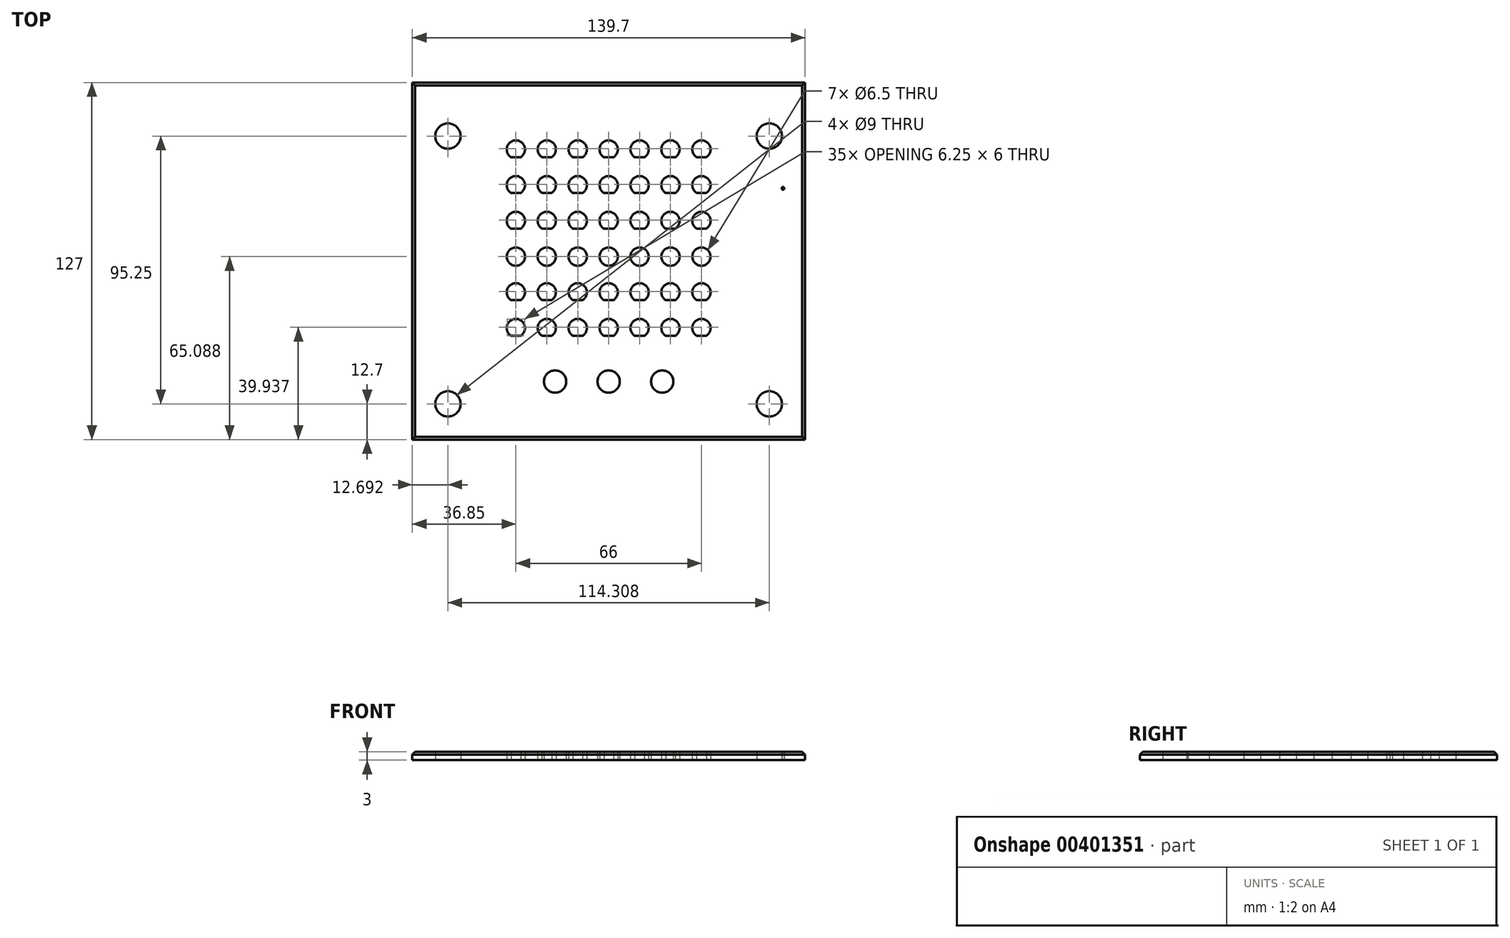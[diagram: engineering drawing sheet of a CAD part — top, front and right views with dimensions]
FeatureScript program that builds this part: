
annotation { "Feature Type Name" : "Feature", "Feature Type Description" : "" }
export const myFeature = defineFeature(function(context is Context, id is Id, definition is map)
    precondition{}
    {
        {
            var Q0;
            Q0=qCreatedBy(makeId("Top.planeOp"),FACE);
            var sketch = newSketch(context, id + "F0", { "sketchPlane" : qUnion([Q0])});
            skLineSegment(sketch, "E0.bottom", {"start": v(69.85, -63.5) * mm, "end": v(-69.85, -63.5) * mm});
            skLineSegment(sketch, "E0.top", {"start": v(69.85, 63.5) * mm, "end": v(-69.85, 63.5) * mm});
            skLineSegment(sketch, "E0.left", {"start": v(69.85, -63.5) * mm, "end": v(69.85, 63.5) * mm});
            skLineSegment(sketch, "E0.right", {"start": v(-69.85, -63.5) * mm, "end": v(-69.85, 63.5) * mm});
            skPoint(sketch, "E0.middle", {"position": v(0, 0) * mm});
            skLineSegment(sketch, "E1", {"start": v(-36.63, 14.29) * mm, "end": v(37.18, 14.29) * mm, "construction": true});
            skLineSegment(sketch, "E2", {"start": v(-37.34, 1.59) * mm, "end": v(37.24, 1.59) * mm, "construction": true});
            skLineSegment(sketch, "E3", {"start": v(-37.24, -11.11) * mm, "end": v(37.24, -11.11) * mm, "construction": true});
            skLineSegment(sketch, "E4", {"start": v(-37.55, -23.81) * mm, "end": v(37.34, -23.81) * mm, "construction": true});
            skLineSegment(sketch, "E5", {"start": v(0, -38.04) * mm, "end": v(0, 63.5) * mm, "construction": true});
            skLineSegment(sketch, "E6", {"start": v(-11, -26.1) * mm, "end": v(-11, 63.5) * mm, "construction": true});
            skLineSegment(sketch, "E7", {"start": v(-22, -38.04) * mm, "end": v(-22, 63.5) * mm, "construction": true});
            skLineSegment(sketch, "E8", {"start": v(-33, -38.57) * mm, "end": v(-33, 63.5) * mm, "construction": true});
            skLineSegment(sketch, "E9", {"start": v(11, -39.12) * mm, "end": v(11, 63.5) * mm, "construction": true});
            skLineSegment(sketch, "E10", {"start": v(22, -39.12) * mm, "end": v(22, 63.5) * mm, "construction": true});
            skLineSegment(sketch, "E11", {"start": v(33, -26.65) * mm, "end": v(33, 63.5) * mm, "construction": true});
            skLineSegment(sketch, "E12", {"start": v(-36.74, -42.86) * mm, "end": v(36.74, -42.86) * mm, "construction": true});
            skPoint(sketch, "E13", {"position": v(0, -42.86) * mm});
            skCircle(sketch, "E14", {"center": v(0, -42.86) * mm, "radius": 3.97 * mm});
            skCircle(sketch, "E15", {"center": v(19.05, -42.86) * mm, "radius": 3.97 * mm});
            skCircle(sketch, "E16", {"center": v(-19.05, -42.86) * mm, "radius": 3.97 * mm});
            skLineSegment(sketch, "E17.bottom", {"start": v(38.1, -38.1) * mm, "end": v(-38.1, -38.1) * mm, "construction": true});
            skLineSegment(sketch, "E17.left", {"start": v(38.1, -38.1) * mm, "end": v(38.1, 38.1) * mm, "construction": true});
            skLineSegment(sketch, "E17.right", {"start": v(-38.1, -38.1) * mm, "end": v(-38.1, 38.1) * mm, "construction": true});
            skCircle(sketch, "E18", {"center": v(-57.15, -50.8) * mm, "radius": 4.5 * mm});
            skLineSegment(sketch, "E19", {"start": v(-57.15, -47.32) * mm, "end": v(-57.15, 45.96) * mm, "construction": true});
            skLineSegment(sketch, "E20", {"start": v(-65.5, -50.8) * mm, "end": v(68.65, -50.8) * mm, "construction": true});
            skLineSegment(sketch, "E21", {"start": v(57.15, -46.6) * mm, "end": v(57.15, 47.13) * mm, "construction": true});
            skLineSegment(sketch, "E22", {"start": v(-64.4, 39.69) * mm, "end": v(66.43, 39.69) * mm, "construction": true});
            skCircle(sketch, "E23", {"center": v(57.15, -50.8) * mm, "radius": 4.5 * mm});
            skLineSegment(sketch, "E24", {"start": v(-36.54, 26.99) * mm, "end": v(36.58, 26.99) * mm, "construction": true});
            skLineSegment(sketch, "E25", {"start": v(-36.46, 39.69) * mm, "end": v(36.58, 39.69) * mm, "construction": true});
            skCircle(sketch, "E26", {"center": v(-33, 39.69) * mm, "radius": 3.25 * mm});
            skLineSegment(sketch, "E27", {"start": v(-67.5, 46.04) * mm, "end": v(65.6, 46.04) * mm, "construction": true});
            skLineSegment(sketch, "E28", {"start": v(-34.73, 36.94) * mm, "end": v(-31.27, 36.94) * mm});
            skCircle(sketch, "E29", {"center": v(-22, 39.69) * mm, "radius": 3.25 * mm});
            skLineSegment(sketch, "E30", {"start": v(-23.73, 36.94) * mm, "end": v(-20.27, 36.94) * mm});
            skCircle(sketch, "E31", {"center": v(-11, 39.69) * mm, "radius": 3.25 * mm});
            skLineSegment(sketch, "E32", {"start": v(-12.73, 36.94) * mm, "end": v(-9.27, 36.94) * mm});
            skCircle(sketch, "E33", {"center": v(0, 39.69) * mm, "radius": 3.25 * mm});
            skLineSegment(sketch, "E34", {"start": v(-1.73, 36.94) * mm, "end": v(1.73, 36.94) * mm});
            skPoint(sketch, "E35", {"position": v(1.02, 39.69) * mm});
            skCircle(sketch, "E36", {"center": v(11, 39.69) * mm, "radius": 3.25 * mm});
            skLineSegment(sketch, "E37", {"start": v(9.27, 36.94) * mm, "end": v(12.73, 36.94) * mm});
            skCircle(sketch, "E38", {"center": v(22, 39.69) * mm, "radius": 3.25 * mm});
            skLineSegment(sketch, "E39", {"start": v(20.27, 36.94) * mm, "end": v(23.73, 36.94) * mm});
            skCircle(sketch, "E40", {"center": v(33, 39.69) * mm, "radius": 3.25 * mm});
            skLineSegment(sketch, "E41", {"start": v(31.27, 36.94) * mm, "end": v(34.73, 36.94) * mm});
            skCircle(sketch, "E42", {"center": v(-33, 26.99) * mm, "radius": 3.25 * mm});
            skLineSegment(sketch, "E43", {"start": v(-34.73, 24.24) * mm, "end": v(-31.27, 24.24) * mm});
            skCircle(sketch, "E44", {"center": v(-22, 26.99) * mm, "radius": 3.25 * mm});
            skLineSegment(sketch, "E45", {"start": v(-23.73, 24.24) * mm, "end": v(-20.27, 24.24) * mm});
            skCircle(sketch, "E46", {"center": v(-11, 26.99) * mm, "radius": 3.25 * mm});
            skLineSegment(sketch, "E47", {"start": v(-12.73, 24.24) * mm, "end": v(-9.27, 24.24) * mm});
            skCircle(sketch, "E48", {"center": v(0, 26.99) * mm, "radius": 3.25 * mm});
            skLineSegment(sketch, "E49", {"start": v(-1.73, 24.24) * mm, "end": v(1.73, 24.24) * mm});
            skCircle(sketch, "E50", {"center": v(11, 26.99) * mm, "radius": 3.25 * mm});
            skLineSegment(sketch, "E51", {"start": v(9.27, 24.24) * mm, "end": v(12.73, 24.24) * mm});
            skCircle(sketch, "E52", {"center": v(22, 26.99) * mm, "radius": 3.25 * mm});
            skLineSegment(sketch, "E53", {"start": v(20.27, 24.24) * mm, "end": v(23.73, 24.24) * mm});
            skCircle(sketch, "E54", {"center": v(33, 26.99) * mm, "radius": 3.25 * mm});
            skLineSegment(sketch, "E55", {"start": v(31.27, 24.24) * mm, "end": v(34.73, 24.24) * mm});
            skPoint(sketch, "E56", {"position": v(0.02, 26.99) * mm});
            skCircle(sketch, "E57", {"center": v(-11, 14.29) * mm, "radius": 3.25 * mm});
            skLineSegment(sketch, "E58", {"start": v(-12.73, 11.54) * mm, "end": v(-9.27, 11.54) * mm});
            skCircle(sketch, "E59", {"center": v(0, 14.29) * mm, "radius": 3.25 * mm});
            skLineSegment(sketch, "E60", {"start": v(-1.73, 11.54) * mm, "end": v(1.73, 11.54) * mm});
            skCircle(sketch, "E61", {"center": v(11, 14.29) * mm, "radius": 3.25 * mm});
            skLineSegment(sketch, "E62", {"start": v(9.27, 11.54) * mm, "end": v(12.73, 11.54) * mm});
            skCircle(sketch, "E63", {"center": v(22, 14.29) * mm, "radius": 3.25 * mm});
            skLineSegment(sketch, "E64", {"start": v(20.27, 11.54) * mm, "end": v(23.73, 11.54) * mm});
            skCircle(sketch, "E65", {"center": v(33, 14.29) * mm, "radius": 3.25 * mm});
            skLineSegment(sketch, "E66", {"start": v(31.27, 11.54) * mm, "end": v(34.73, 11.54) * mm});
            skCircle(sketch, "E67", {"center": v(-33, 14.29) * mm, "radius": 3.25 * mm});
            skLineSegment(sketch, "E68", {"start": v(-34.73, 11.54) * mm, "end": v(-31.27, 11.54) * mm});
            skCircle(sketch, "E69", {"center": v(-22, 14.29) * mm, "radius": 3.25 * mm});
            skLineSegment(sketch, "E70", {"start": v(-23.73, 11.54) * mm, "end": v(-20.27, 11.54) * mm});
            skCircle(sketch, "E71", {"center": v(-11, -11.11) * mm, "radius": 3.25 * mm});
            skLineSegment(sketch, "E72", {"start": v(-12.73, -13.86) * mm, "end": v(-9.27, -13.86) * mm});
            skCircle(sketch, "E73", {"center": v(0, -11.11) * mm, "radius": 3.25 * mm});
            skLineSegment(sketch, "E74", {"start": v(-1.73, -13.86) * mm, "end": v(1.73, -13.86) * mm});
            skCircle(sketch, "E75", {"center": v(11, -11.11) * mm, "radius": 3.25 * mm});
            skLineSegment(sketch, "E76", {"start": v(9.27, -13.86) * mm, "end": v(12.73, -13.86) * mm});
            skCircle(sketch, "E77", {"center": v(22, -11.11) * mm, "radius": 3.25 * mm});
            skLineSegment(sketch, "E78", {"start": v(20.27, -13.86) * mm, "end": v(23.73, -13.86) * mm});
            skCircle(sketch, "E79", {"center": v(33, -11.11) * mm, "radius": 3.25 * mm});
            skLineSegment(sketch, "E80", {"start": v(31.27, -13.86) * mm, "end": v(34.73, -13.86) * mm});
            skCircle(sketch, "E81", {"center": v(-33, -11.11) * mm, "radius": 3.25 * mm});
            skLineSegment(sketch, "E82", {"start": v(-34.73, -13.86) * mm, "end": v(-31.27, -13.86) * mm});
            skCircle(sketch, "E83", {"center": v(-22, -11.11) * mm, "radius": 3.25 * mm});
            skLineSegment(sketch, "E84", {"start": v(-23.73, -13.86) * mm, "end": v(-20.27, -13.86) * mm});
            skCircle(sketch, "E85", {"center": v(-11, -23.81) * mm, "radius": 3.25 * mm});
            skLineSegment(sketch, "E86", {"start": v(-12.73, -26.56) * mm, "end": v(-9.27, -26.56) * mm});
            skCircle(sketch, "E87", {"center": v(0, -23.81) * mm, "radius": 3.25 * mm});
            skLineSegment(sketch, "E88", {"start": v(-1.73, -26.56) * mm, "end": v(1.73, -26.56) * mm});
            skCircle(sketch, "E89", {"center": v(11, -23.81) * mm, "radius": 3.25 * mm});
            skLineSegment(sketch, "E90", {"start": v(9.27, -26.56) * mm, "end": v(12.73, -26.56) * mm});
            skCircle(sketch, "E91", {"center": v(22, -23.81) * mm, "radius": 3.25 * mm});
            skLineSegment(sketch, "E92", {"start": v(20.27, -26.56) * mm, "end": v(23.73, -26.56) * mm});
            skCircle(sketch, "E93", {"center": v(33, -23.81) * mm, "radius": 3.25 * mm});
            skLineSegment(sketch, "E94", {"start": v(31.27, -26.56) * mm, "end": v(34.73, -26.56) * mm});
            skLineSegment(sketch, "E95", {"start": v(-33, -23.81) * mm, "end": v(-29.54, -23.81) * mm});
            skCircle(sketch, "E96", {"center": v(-22, -23.81) * mm, "radius": 3.25 * mm});
            skLineSegment(sketch, "E97", {"start": v(-23.73, -26.56) * mm, "end": v(-20.27, -26.56) * mm});
            skCircle(sketch, "E98", {"center": v(-33, -23.81) * mm, "radius": 3.25 * mm});
            skLineSegment(sketch, "E99", {"start": v(-34.73, -26.56) * mm, "end": v(-31.27, -26.56) * mm});
            skCircle(sketch, "E100", {"center": v(57.15, 44.45) * mm, "radius": 4.5 * mm});
            skCircle(sketch, "E101", {"center": v(61.99, 25.86) * mm, "radius": 0.47 * mm});
            skCircle(sketch, "E102", {"center": v(-57.16, 44.45) * mm, "radius": 4.5 * mm});
            skCircle(sketch, "E103", {"center": v(-11, 1.59) * mm, "radius": 3.25 * mm});
            skLineSegment(sketch, "E104", {"start": v(-12.73, -1.16) * mm, "end": v(-9.27, -1.16) * mm});
            skCircle(sketch, "E105", {"center": v(0, 1.59) * mm, "radius": 3.25 * mm});
            skLineSegment(sketch, "E106", {"start": v(-1.73, -1.16) * mm, "end": v(1.73, -1.16) * mm});
            skCircle(sketch, "E107", {"center": v(-33, 1.59) * mm, "radius": 3.25 * mm});
            skLineSegment(sketch, "E108", {"start": v(-34.73, -1.16) * mm, "end": v(-31.27, -1.16) * mm});
            skCircle(sketch, "E109", {"center": v(-22, 1.59) * mm, "radius": 3.25 * mm});
            skLineSegment(sketch, "E110", {"start": v(-23.73, -1.16) * mm, "end": v(-20.27, -1.16) * mm});
            skCircle(sketch, "E111", {"center": v(11, 1.59) * mm, "radius": 3.25 * mm});
            skLineSegment(sketch, "E112", {"start": v(9.27, -1.16) * mm, "end": v(12.73, -1.16) * mm});
            skCircle(sketch, "E113", {"center": v(22, 1.59) * mm, "radius": 3.25 * mm});
            skLineSegment(sketch, "E114", {"start": v(20.27, -1.16) * mm, "end": v(23.73, -1.16) * mm});
            skCircle(sketch, "E115", {"center": v(33, 1.59) * mm, "radius": 3.25 * mm});
            skLineSegment(sketch, "E116", {"start": v(31.27, -1.16) * mm, "end": v(34.73, -1.16) * mm});
            skSolve(sketch);
        }
        {
            var Q0;
            {var subQ0=sQuery(id+"F0.wireOp",EDGE,"E28");Q0=makeQuery(id+"F0.imprint","IMPRINT",FACE,{"disambiguationData":[TD([[makeQuery(id+"F0.imprint","IMPRINT",EDGE,{"derivedFrom":subQ0}),-1.0]])]});}
            var Q1;
            {var subQ0=sQuery(id+"F0.wireOp",EDGE,"E30");Q1=makeQuery(id+"F0.imprint","IMPRINT",FACE,{"disambiguationData":[TD([[makeQuery(id+"F0.imprint","IMPRINT",EDGE,{"derivedFrom":subQ0}),-1.0]])]});}
            var Q2;
            {var subQ0=sQuery(id+"F0.wireOp",EDGE,"E32");Q2=makeQuery(id+"F0.imprint","IMPRINT",FACE,{"disambiguationData":[TD([[makeQuery(id+"F0.imprint","IMPRINT",EDGE,{"derivedFrom":subQ0}),-1.0]])]});}
            var Q3;
            {var subQ0=sQuery(id+"F0.wireOp",EDGE,"E34");Q3=makeQuery(id+"F0.imprint","IMPRINT",FACE,{"disambiguationData":[TD([[makeQuery(id+"F0.imprint","IMPRINT",EDGE,{"derivedFrom":subQ0}),-1.0]])]});}
            var Q4;
            {var subQ0=sQuery(id+"F0.wireOp",EDGE,"E49");Q4=makeQuery(id+"F0.imprint","IMPRINT",FACE,{"disambiguationData":[TD([[makeQuery(id+"F0.imprint","IMPRINT",EDGE,{"derivedFrom":subQ0}),-1.0]])]});}
            var Q5;
            {var subQ0=sQuery(id+"F0.wireOp",EDGE,"E47");Q5=makeQuery(id+"F0.imprint","IMPRINT",FACE,{"disambiguationData":[TD([[makeQuery(id+"F0.imprint","IMPRINT",EDGE,{"derivedFrom":subQ0}),-1.0]])]});}
            var Q6;
            {var subQ0=sQuery(id+"F0.wireOp",EDGE,"E45");Q6=makeQuery(id+"F0.imprint","IMPRINT",FACE,{"disambiguationData":[TD([[makeQuery(id+"F0.imprint","IMPRINT",EDGE,{"derivedFrom":subQ0}),-1.0]])]});}
            var Q7;
            {var subQ0=sQuery(id+"F0.wireOp",EDGE,"E43");Q7=makeQuery(id+"F0.imprint","IMPRINT",FACE,{"disambiguationData":[TD([[makeQuery(id+"F0.imprint","IMPRINT",EDGE,{"derivedFrom":subQ0}),-1.0]])]});}
            var Q8;
            {var subQ0=sQuery(id+"F0.wireOp",EDGE,"E37");Q8=makeQuery(id+"F0.imprint","IMPRINT",FACE,{"disambiguationData":[TD([[makeQuery(id+"F0.imprint","IMPRINT",EDGE,{"derivedFrom":subQ0}),-1.0]])]});}
            var Q9;
            {var subQ0=sQuery(id+"F0.wireOp",EDGE,"E39");Q9=makeQuery(id+"F0.imprint","IMPRINT",FACE,{"disambiguationData":[TD([[makeQuery(id+"F0.imprint","IMPRINT",EDGE,{"derivedFrom":subQ0}),-1.0]])]});}
            var Q10;
            {var subQ0=sQuery(id+"F0.wireOp",EDGE,"E41");Q10=makeQuery(id+"F0.imprint","IMPRINT",FACE,{"disambiguationData":[TD([[makeQuery(id+"F0.imprint","IMPRINT",EDGE,{"derivedFrom":subQ0}),-1.0]])]});}
            var Q11;
            {var subQ0=sQuery(id+"F0.wireOp",EDGE,"E55");Q11=makeQuery(id+"F0.imprint","IMPRINT",FACE,{"disambiguationData":[TD([[makeQuery(id+"F0.imprint","IMPRINT",EDGE,{"derivedFrom":subQ0}),-1.0]])]});}
            var Q12;
            {var subQ0=sQuery(id+"F0.wireOp",EDGE,"E53");Q12=makeQuery(id+"F0.imprint","IMPRINT",FACE,{"disambiguationData":[TD([[makeQuery(id+"F0.imprint","IMPRINT",EDGE,{"derivedFrom":subQ0}),-1.0]])]});}
            var Q13;
            {var subQ0=sQuery(id+"F0.wireOp",EDGE,"E51");Q13=makeQuery(id+"F0.imprint","IMPRINT",FACE,{"disambiguationData":[TD([[makeQuery(id+"F0.imprint","IMPRINT",EDGE,{"derivedFrom":subQ0}),-1.0]])]});}
            var Q14;
            {var subQ0=sQuery(id+"F0.wireOp",EDGE,"E66");Q14=makeQuery(id+"F0.imprint","IMPRINT",FACE,{"disambiguationData":[TD([[makeQuery(id+"F0.imprint","IMPRINT",EDGE,{"derivedFrom":subQ0}),-1.0]])]});}
            var Q15;
            {var subQ0=sQuery(id+"F0.wireOp",EDGE,"5e4bbd30-fef1-421a-bd2a-7a05320ef783");Q15=makeQuery(id+"F0.imprint","IMPRINT",FACE,{"disambiguationData":[TD([[makeQuery(id+"F0.imprint","IMPRINT",EDGE,{"derivedFrom":subQ0}),-1.0]])]});}
            var Q16;
            {var subQ0=sQuery(id+"F0.wireOp",EDGE,"9f2551cd-3248-4687-9eb7-92e1bf331b68");Q16=makeQuery(id+"F0.imprint","IMPRINT",FACE,{"disambiguationData":[TD([[makeQuery(id+"F0.imprint","IMPRINT",EDGE,{"derivedFrom":subQ0}),-1.0]])]});}
            var Q17;
            {var subQ0=sQuery(id+"F0.wireOp",EDGE,"ff4b2a3b-82b4-439a-97c0-e02cae182584");Q17=makeQuery(id+"F0.imprint","IMPRINT",FACE,{"disambiguationData":[TD([[makeQuery(id+"F0.imprint","IMPRINT",EDGE,{"derivedFrom":subQ0}),-1.0]])]});}
            var Q18;
            {var subQ0=sQuery(id+"F0.wireOp",EDGE,"E62");Q18=makeQuery(id+"F0.imprint","IMPRINT",FACE,{"disambiguationData":[TD([[makeQuery(id+"F0.imprint","IMPRINT",EDGE,{"derivedFrom":subQ0}),-1.0]])]});}
            var Q19;
            {var subQ0=sQuery(id+"F0.wireOp",EDGE,"E64");Q19=makeQuery(id+"F0.imprint","IMPRINT",FACE,{"disambiguationData":[TD([[makeQuery(id+"F0.imprint","IMPRINT",EDGE,{"derivedFrom":subQ0}),-1.0]])]});}
            var Q20;
            {var subQ0=sQuery(id+"F0.wireOp",EDGE,"E60");Q20=makeQuery(id+"F0.imprint","IMPRINT",FACE,{"disambiguationData":[TD([[makeQuery(id+"F0.imprint","IMPRINT",EDGE,{"derivedFrom":subQ0}),-1.0]])]});}
            var Q21;
            {var subQ0=sQuery(id+"F0.wireOp",EDGE,"c00b9fa8-b2ed-4572-8b60-42da16ad9391");Q21=makeQuery(id+"F0.imprint","IMPRINT",FACE,{"disambiguationData":[TD([[makeQuery(id+"F0.imprint","IMPRINT",EDGE,{"derivedFrom":subQ0}),-1.0]])]});}
            var Q22;
            {var subQ0=sQuery(id+"F0.wireOp",EDGE,"ec62a128-463b-493f-a66a-9174ab87ccfa");Q22=makeQuery(id+"F0.imprint","IMPRINT",FACE,{"disambiguationData":[TD([[makeQuery(id+"F0.imprint","IMPRINT",EDGE,{"derivedFrom":subQ0}),-1.0]])]});}
            var Q23;
            {var subQ0=sQuery(id+"F0.wireOp",EDGE,"E58");Q23=makeQuery(id+"F0.imprint","IMPRINT",FACE,{"disambiguationData":[TD([[makeQuery(id+"F0.imprint","IMPRINT",EDGE,{"derivedFrom":subQ0}),-1.0]])]});}
            var Q24;
            {var subQ0=sQuery(id+"F0.wireOp",EDGE,"E70");Q24=makeQuery(id+"F0.imprint","IMPRINT",FACE,{"disambiguationData":[TD([[makeQuery(id+"F0.imprint","IMPRINT",EDGE,{"derivedFrom":subQ0}),-1.0]])]});}
            var Q25;
            {var subQ0=sQuery(id+"F0.wireOp",EDGE,"82e3a988-f3b1-45aa-923b-77cc7cc4a563");Q25=makeQuery(id+"F0.imprint","IMPRINT",FACE,{"disambiguationData":[TD([[makeQuery(id+"F0.imprint","IMPRINT",EDGE,{"derivedFrom":subQ0}),-1.0]])]});}
            var Q26;
            {var subQ0=sQuery(id+"F0.wireOp",EDGE,"1198471f-dd7b-475d-a34b-8bf7346cd8f1");Q26=makeQuery(id+"F0.imprint","IMPRINT",FACE,{"disambiguationData":[TD([[makeQuery(id+"F0.imprint","IMPRINT",EDGE,{"derivedFrom":subQ0}),-1.0]])]});}
            var Q27;
            {var subQ0=sQuery(id+"F0.wireOp",EDGE,"E68");Q27=makeQuery(id+"F0.imprint","IMPRINT",FACE,{"disambiguationData":[TD([[makeQuery(id+"F0.imprint","IMPRINT",EDGE,{"derivedFrom":subQ0}),-1.0]])]});}
            var Q28;
            {var subQ0=sQuery(id+"F0.wireOp",EDGE,"E82");Q28=makeQuery(id+"F0.imprint","IMPRINT",FACE,{"disambiguationData":[TD([[makeQuery(id+"F0.imprint","IMPRINT",EDGE,{"derivedFrom":subQ0}),-1.0]])]});}
            var Q29;
            {var subQ0=sQuery(id+"F0.wireOp",EDGE,"E99");Q29=makeQuery(id+"F0.imprint","IMPRINT",FACE,{"disambiguationData":[TD([[makeQuery(id+"F0.imprint","IMPRINT",EDGE,{"derivedFrom":subQ0}),-1.0]])]});}
            var Q30;
            {var subQ0=sQuery(id+"F0.wireOp",EDGE,"E97");Q30=makeQuery(id+"F0.imprint","IMPRINT",FACE,{"disambiguationData":[TD([[makeQuery(id+"F0.imprint","IMPRINT",EDGE,{"derivedFrom":subQ0}),-1.0]])]});}
            var Q31;
            {var subQ0=sQuery(id+"F0.wireOp",EDGE,"E84");Q31=makeQuery(id+"F0.imprint","IMPRINT",FACE,{"disambiguationData":[TD([[makeQuery(id+"F0.imprint","IMPRINT",EDGE,{"derivedFrom":subQ0}),-1.0]])]});}
            var Q32;
            {var subQ0=sQuery(id+"F0.wireOp",EDGE,"E72");Q32=makeQuery(id+"F0.imprint","IMPRINT",FACE,{"disambiguationData":[TD([[makeQuery(id+"F0.imprint","IMPRINT",EDGE,{"derivedFrom":subQ0}),-1.0]])]});}
            var Q33;
            {var subQ0=sQuery(id+"F0.wireOp",EDGE,"E86");Q33=makeQuery(id+"F0.imprint","IMPRINT",FACE,{"disambiguationData":[TD([[makeQuery(id+"F0.imprint","IMPRINT",EDGE,{"derivedFrom":subQ0}),-1.0]])]});}
            var Q34;
            {var subQ0=sQuery(id+"F0.wireOp",EDGE,"E88");Q34=makeQuery(id+"F0.imprint","IMPRINT",FACE,{"disambiguationData":[TD([[makeQuery(id+"F0.imprint","IMPRINT",EDGE,{"derivedFrom":subQ0}),-1.0]])]});}
            var Q35;
            {var subQ0=sQuery(id+"F0.wireOp",EDGE,"E74");Q35=makeQuery(id+"F0.imprint","IMPRINT",FACE,{"disambiguationData":[TD([[makeQuery(id+"F0.imprint","IMPRINT",EDGE,{"derivedFrom":subQ0}),-1.0]])]});}
            var Q36;
            {var subQ0=sQuery(id+"F0.wireOp",EDGE,"E76");Q36=makeQuery(id+"F0.imprint","IMPRINT",FACE,{"disambiguationData":[TD([[makeQuery(id+"F0.imprint","IMPRINT",EDGE,{"derivedFrom":subQ0}),-1.0]])]});}
            var Q37;
            {var subQ0=sQuery(id+"F0.wireOp",EDGE,"E78");Q37=makeQuery(id+"F0.imprint","IMPRINT",FACE,{"disambiguationData":[TD([[makeQuery(id+"F0.imprint","IMPRINT",EDGE,{"derivedFrom":subQ0}),-1.0]])]});}
            var Q38;
            {var subQ0=sQuery(id+"F0.wireOp",EDGE,"E80");Q38=makeQuery(id+"F0.imprint","IMPRINT",FACE,{"disambiguationData":[TD([[makeQuery(id+"F0.imprint","IMPRINT",EDGE,{"derivedFrom":subQ0}),-1.0]])]});}
            var Q39;
            {var subQ0=sQuery(id+"F0.wireOp",EDGE,"E94");Q39=makeQuery(id+"F0.imprint","IMPRINT",FACE,{"disambiguationData":[TD([[makeQuery(id+"F0.imprint","IMPRINT",EDGE,{"derivedFrom":subQ0}),-1.0]])]});}
            var Q40;
            {var subQ0=sQuery(id+"F0.wireOp",EDGE,"E92");Q40=makeQuery(id+"F0.imprint","IMPRINT",FACE,{"disambiguationData":[TD([[makeQuery(id+"F0.imprint","IMPRINT",EDGE,{"derivedFrom":subQ0}),-1.0]])]});}
            var Q41;
            {var subQ0=sQuery(id+"F0.wireOp",EDGE,"E90");Q41=makeQuery(id+"F0.imprint","IMPRINT",FACE,{"disambiguationData":[TD([[makeQuery(id+"F0.imprint","IMPRINT",EDGE,{"derivedFrom":subQ0}),-1.0]])]});}
            var Q42;
            Q42=makeQuery(id+"F0.imprint","IMPRINT",FACE,{"disambiguationData":[TD([[makeQuery(id+"F0.imprint","IMPRINT",EDGE,{"derivedFrom":sQuery(id+"F0.wireOp",EDGE,"E0.bottom")}),-1.0]])]});
            extrude(context, id + "F1", {"entities" : qUnion([Q0, Q1, Q2, Q3, Q4, Q5, Q6, Q7, Q8, Q9, Q10, Q11, Q12, Q13, Q14, Q15, Q16, Q17, Q18, Q19, Q20, Q21, Q22, Q23, Q24, Q25, Q26, Q27, Q28, Q29, Q30, Q31, Q32, Q33, Q34, Q35, Q36, Q37, Q38, Q39, Q40, Q41, Q42]), "depth" : 3 * mm, "offsetDistance" : 25 * mm});
        }
        {
            var Q0;
            Q0=makeQuery(id+"F1.opExtrude","CAP_EDGE",EDGE,{"disambiguationData":[OSD([sQuery(id+"F0.wireOp",EDGE,"E0.right")])],"isStart":false});
            var Q1;
            Q1=makeQuery(id+"F1.opExtrude","CAP_EDGE",EDGE,{"disambiguationData":[OSD([sQuery(id+"F0.wireOp",EDGE,"E0.bottom")])],"isStart":false});
            var Q2;
            Q2=makeQuery(id+"F1.opExtrude","CAP_EDGE",EDGE,{"disambiguationData":[OSD([sQuery(id+"F0.wireOp",EDGE,"E0.left")])],"isStart":false});
            var Q3;
            Q3=makeQuery(id+"F1.opExtrude","CAP_EDGE",EDGE,{"disambiguationData":[OSD([sQuery(id+"F0.wireOp",EDGE,"E0.top")])],"isStart":false});
            chamfer(context, id + "F2", {"entities" : qUnion([Q0, Q1, Q2, Q3]), "width" : 1 * mm, "tangentPropagation" : true});
        }
    });
